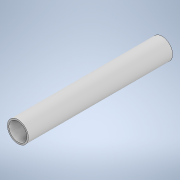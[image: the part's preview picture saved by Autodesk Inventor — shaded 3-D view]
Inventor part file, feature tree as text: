
AUTODESK INVENTOR PART (.ipt)
format: ipt  version: 2022.2 (Build 262287000, 287)  size: 96,256 bytes
history: native  units: in
note: dims shown in document units (in); Inventor stores cm internally (conversion verified against a paired STEP export)
features: extrude x1, sketch x1
ambient origin geometry x8: Origin, YZ Plane, XZ Plane, XY Plane, X Axis, Y Axis, Z Axis, Center Point
bodies: Solid1 (feature_tree)
feature tree (2):
  extrude  "Extrusion1"  Depth=24.0in
  sketch  "Sketch1"  dims[d0=3.5in d1=3.0in d2=24.0in d3=0.0in]
